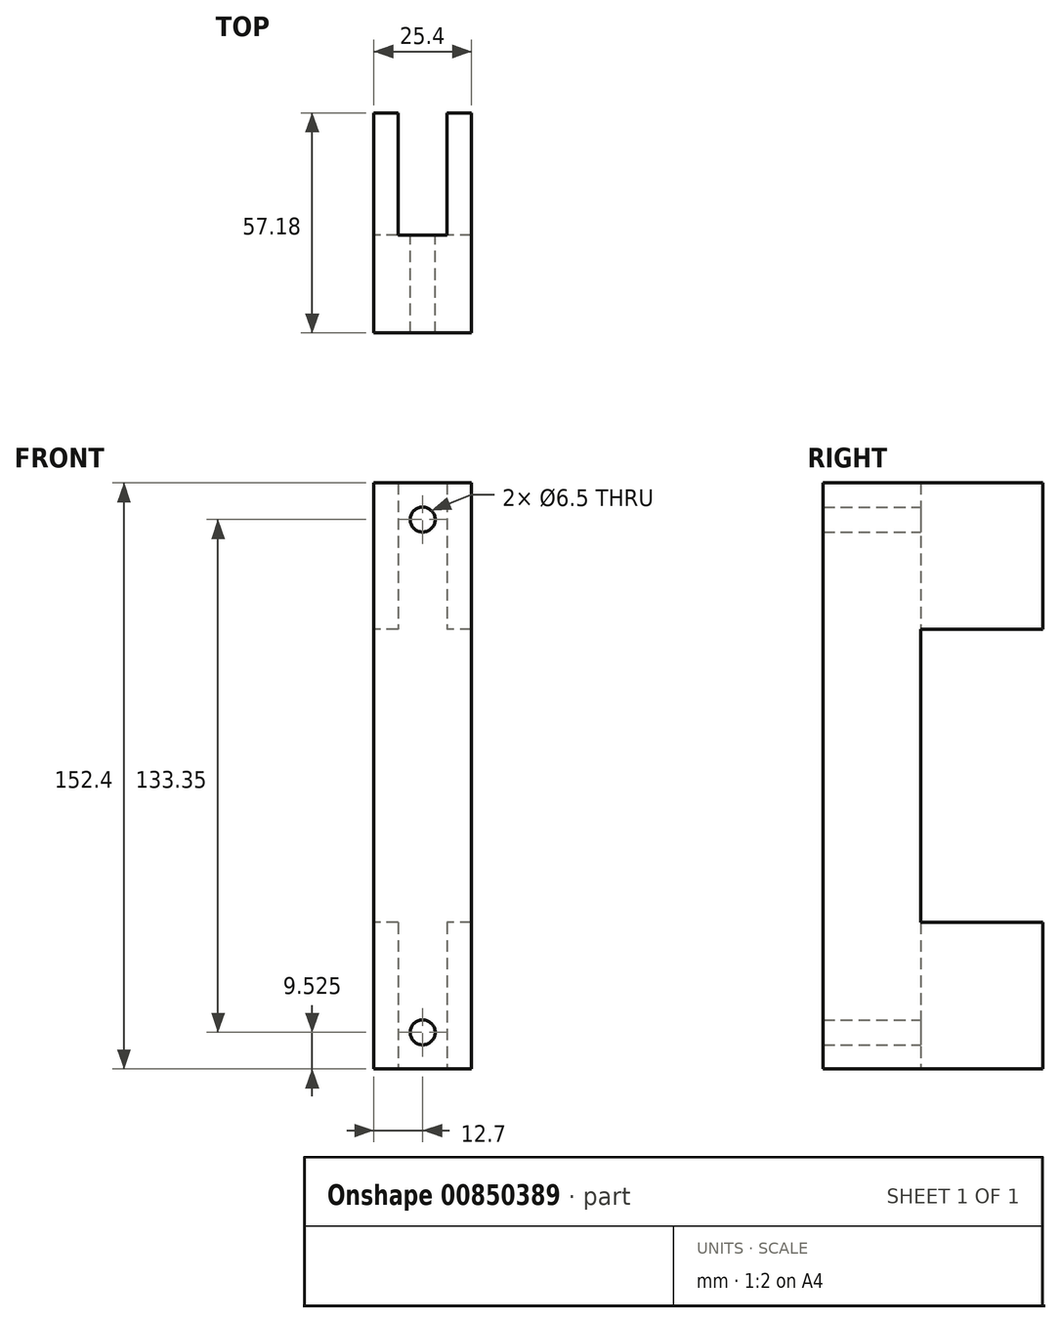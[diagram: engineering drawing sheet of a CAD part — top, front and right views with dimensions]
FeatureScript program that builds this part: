
annotation { "Feature Type Name" : "Feature", "Feature Type Description" : "" }
export const myFeature = defineFeature(function(context is Context, id is Id, definition is map)
    precondition{}
    {
        {
            var Q0;
            Q0=qCreatedBy(makeId("Top.planeOp"),FACE);
            var sketch = newSketch(context, id + "F0", { "sketchPlane" : qUnion([Q0])});
            skLineSegment(sketch, "E0.bottom", {"start": v(12.7, -19.05) * mm, "end": v(-12.7, -19.05) * mm});
            skLineSegment(sketch, "E0.top", {"start": v(12.7, 19.05) * mm, "end": v(-12.7, 19.05) * mm});
            skLineSegment(sketch, "E0.left", {"start": v(12.7, -19.05) * mm, "end": v(12.7, 19.05) * mm});
            skLineSegment(sketch, "E0.right", {"start": v(-12.7, -19.05) * mm, "end": v(-12.7, 19.05) * mm});
            skPoint(sketch, "E0.middle", {"position": v(0, 0) * mm});
            skSolve(sketch);
        }
        {
            var Q0;
            Q0=makeQuery(id+"F0.imprint","IMPRINT",FACE,{"disambiguationData":[TD([[makeQuery(id+"F0.imprint","IMPRINT",EDGE,{"derivedFrom":sQuery(id+"F0.wireOp",EDGE,"E0.bottom")}),-1.0]])]});
            extrude(context, id + "F1", {"entities" : qUnion([Q0]), "depth" : 38.1 * mm, "offsetDistance" : 25 * mm});
        }
        {
            var Q0;
            Q0=makeQuery(id+"F1.opExtrude","SWEPT_FACE",FACE,{"disambiguationData":[OSD([sQuery(id+"F0.wireOp",EDGE,"E0.top")])]});
            var Q1;
            Q1=makeQuery(id+"F1.opExtrude","CAP_FACE",FACE,{"disambiguationData":[OSD([sQuery(id+"F0.wireOp",EDGE,"E0.bottom"),sQuery(id+"F0.wireOp",EDGE,"E0.top"),sQuery(id+"F0.wireOp",EDGE,"E0.left"),sQuery(id+"F0.wireOp",EDGE,"E0.right")])],"isStart":false});
            var Q2;
            Q2=makeQuery(id+"F1.opExtrude","CAP_FACE",FACE,{"disambiguationData":[OSD([sQuery(id+"F0.wireOp",EDGE,"E0.bottom"),sQuery(id+"F0.wireOp",EDGE,"E0.top"),sQuery(id+"F0.wireOp",EDGE,"E0.left"),sQuery(id+"F0.wireOp",EDGE,"E0.right")])],"isStart":true});
            shell(context, id + "F2", {"entities" : qUnion([Q0, Q1, Q2]), "thickness" : 6.33 * mm});
        }
        {
            var Q0;
            Q0=makeQuery(id+"F1.opExtrude","SWEPT_FACE",FACE,{"disambiguationData":[OSD([sQuery(id+"F0.wireOp",EDGE,"E0.bottom")])]});
            extrude(context, id + "F3", {"entities" : qUnion([Q0]), "operationType" : NewBodyOperationType.ADD, "depth" : 19.07 * mm, "offsetDistance" : 25 * mm});
        }
        {
            var Q0;
            {var subQ0=sQuery(id+"F0.wireOp",EDGE,"E0.bottom");Q0=makeQuery(id+"F3.boolean.opBoolean","MERGE",FACE,{"derivedFrom":[makeQuery(id+"F1.opExtrude","CAP_FACE",FACE,{"disambiguationData":[OSD([subQ0,sQuery(id+"F0.wireOp",EDGE,"E0.top"),sQuery(id+"F0.wireOp",EDGE,"E0.left"),sQuery(id+"F0.wireOp",EDGE,"E0.right")])],"isStart":true}),makeQuery(id+"F3.opExtrude","SWEPT_FACE",FACE,{"disambiguationData":[OSD([subQ0]),TDD([makeQuery(id+"F1.opExtrude","CAP_EDGE",EDGE,{"disambiguationData":[OSD([subQ0])],"isStart":true})])]})]});}
            extrude(context, id + "F4", {"entities" : qUnion([Q0]), "operationType" : NewBodyOperationType.ADD, "depth" : 114.3 * mm, "offsetDistance" : 25 * mm});
        }
        {
            var Q0;
            {var subQ0=sQuery(id+"F0.wireOp",EDGE,"E0.bottom");Q0=makeQuery(id+"F4.boolean.opBoolean","MERGE",FACE,{"derivedFrom":[makeQuery(id+"F2.opShell","OFFSET_FACE",FACE,{"disambiguationData":[OSD([subQ0])]}),makeQuery(id+"F4.opExtrude","SWEPT_FACE",FACE,{"disambiguationData":[OSD([subQ0]),TDD([makeQuery(id+"F2.opShell","OFFSET_EDGE",EDGE,{"disambiguationData":[OSD([subQ0]),TDD([makeQuery(id+"F1.opExtrude","CAP_EDGE",EDGE,{"disambiguationData":[OSD([subQ0])],"isStart":true})])]})])]})]});}
            var sketch = newSketch(context, id + "F5", { "sketchPlane" : qUnion([Q0])});
            skPoint(sketch, "E1", {"position": v(0, -104.78) * mm});
            skPoint(sketch, "E1.positionSnap0", {"position": v(0, -114.3) * mm});
            skPoint(sketch, "E2", {"position": v(0, 28.58) * mm});
            skPoint(sketch, "E2.positionSnap0", {"position": v(0, 38.1) * mm});
            skSolve(sketch);
        }
        {
            var Q0;
            Q0=sQuery(id+"F5.wireOp",VERTEX,"E1");
            var Q1;
            Q1=sQuery(id+"F5.wireOp",VERTEX,"E2");
            var Q2;
            Q2=makeQuery(id+"F1.opExtrude","SWEPT_BODY",BODY,{"disambiguationData":[OSD([sQuery(id+"F0.wireOp",EDGE,"E0.bottom"),sQuery(id+"F0.wireOp",EDGE,"E0.top"),sQuery(id+"F0.wireOp",EDGE,"E0.left"),sQuery(id+"F0.wireOp",EDGE,"E0.right")])]});
            hole(context, id + "F6", {"style" : HoleStyle.SIMPLE, "endStyle" : HoleEndStyle.BLIND, "holeDiameter" : 6.5 * mm, "majorDiameter" : 5 * mm, "holeDepth" : 50 * mm, "isTappedThrough" : true, "tappedDepth" : 12 * mm, "tapClearance" : 3, "locations" : qUnion([Q0, Q1]), "scope" : qUnion([Q2])});
        }
        {
            var Q0;
            {var subQ0=sQuery(id+"F0.wireOp",EDGE,"E0.top");Q0=makeQuery(id+"F4.boolean.opBoolean","MERGE",FACE,{"derivedFrom":[makeQuery(id+"F2.opShell","OFFSET_FACE",FACE,{"disambiguationData":[OSD([subQ0])]}),makeQuery(id+"F4.opExtrude","SWEPT_FACE",FACE,{"disambiguationData":[OSD([subQ0]),TDD([makeQuery(id+"F1.opExtrude","CAP_EDGE",EDGE,{"disambiguationData":[OSD([subQ0])],"isStart":true})])]})]});}
            var sketch = newSketch(context, id + "F7", { "sketchPlane" : qUnion([Q0])});
            skLineSegment(sketch, "E3", {"start": v(-12.7, -76.2) * mm, "end": v(-6.38, -76.2) * mm});
            skLineSegment(sketch, "E4", {"start": v(-12.7, 0) * mm, "end": v(-6.38, 0) * mm});
            skSolve(sketch);
        }
        {
            var Q0;
            {var subQ0=sQuery(id+"F0.wireOp",EDGE,"E0.top");Q0=makeQuery(id+"F4.boolean.opBoolean","MERGE",FACE,{"derivedFrom":[makeQuery(id+"F1.opExtrude","SWEPT_FACE",FACE,{"disambiguationData":[OSD([subQ0])]}),makeQuery(id+"F4.opExtrude","SWEPT_FACE",FACE,{"disambiguationData":[OSD([subQ0]),TDD([makeQuery(id+"F2.opShell","OFFSET_EDGE",EDGE,{"disambiguationData":[OSD([subQ0]),TDD([makeQuery(id+"F1.opExtrude","CAP_EDGE",EDGE,{"disambiguationData":[OSD([subQ0])],"isStart":true})])]})])]})]});}
            var sketch = newSketch(context, id + "F8", { "sketchPlane" : qUnion([Q0])});
            skLineSegment(sketch, "E5", {"start": v(6.37, -76.2) * mm, "end": v(12.7, -76.2) * mm});
            skLineSegment(sketch, "E6", {"start": v(6.37, 0) * mm, "end": v(12.7, 0) * mm});
            skSolve(sketch);
        }
        {
            var Q0;
            {var subQ0=sQuery(id+"F7.wireOp",EDGE,"E3");Q0=makeQuery(id+"F7.imprint","IMPRINT",FACE,{"disambiguationData":[TD([[makeQuery(id+"F7.imprint","IMPRINT",EDGE,{"derivedFrom":subQ0}),1.0]])]});}
            var Q1;
            {var subQ0=sQuery(id+"F8.wireOp",EDGE,"E5");Q1=makeQuery(id+"F8.imprint","IMPRINT",FACE,{"disambiguationData":[TD([[makeQuery(id+"F8.imprint","IMPRINT",EDGE,{"derivedFrom":subQ0}),1.0]])]});}
            extrude(context, id + "F9", {"entities" : qUnion([Q0, Q1]), "operationType" : NewBodyOperationType.REMOVE, "oppositeDirection" : true, "depth" : 31.77 * mm, "offsetDistance" : 25 * mm});
        }
    });
